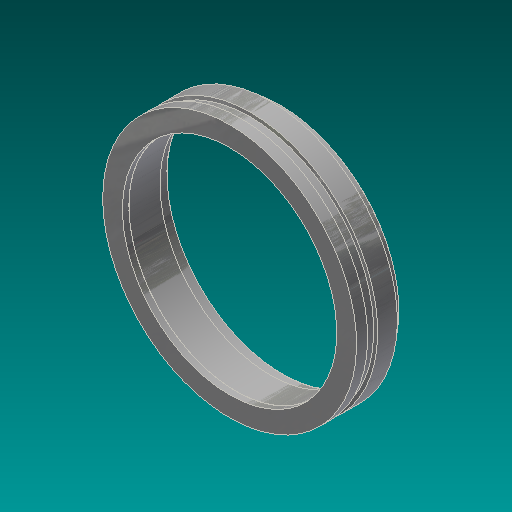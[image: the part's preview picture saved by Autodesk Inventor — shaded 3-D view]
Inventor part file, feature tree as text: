
AUTODESK INVENTOR PART (.ipt)
format: ipt  version: 2017.3 (Build 213257000, 257)  size: 220,672 bytes
history: native  units: in
note: dims shown in document units (in); Inventor stores cm internally (conversion verified against a paired STEP export)
features: revolve x1, chamfer x1, sketch x1
ambient origin geometry x8: Origin, YZ Plane, XZ Plane, XY Plane, X Axis, Y Axis, Z Axis, Center Point
bodies: Solid1 (feature_tree)
feature tree (3):
  revolve  "Revolution1"  [1 undecoded]
  chamfer  "Chamfer2"  Angle=90.0deg  [1 undecoded]
  sketch  "Sketch1"  dims[d0=16.25in d5=1.0in d6=90.0deg d13=18.75in d14=19.25in d16=1.75in d17=1.35in d18=0.0515in d19=0.0842in d20=0.0312in d21=0.125in d22=45.0deg d32=18.0in d33=0.4375in d35=0.0625in d36=0.25in d38=8.0in d44=0.5in d46=0.2577in d47=0.5in d48=16.75in d49=6.1875in]
note: 2 required parameter values undecoded (feature->parameter linkage not recoverable at this tier; creation-order binding heuristic only, values carry confidence <= 0.55)